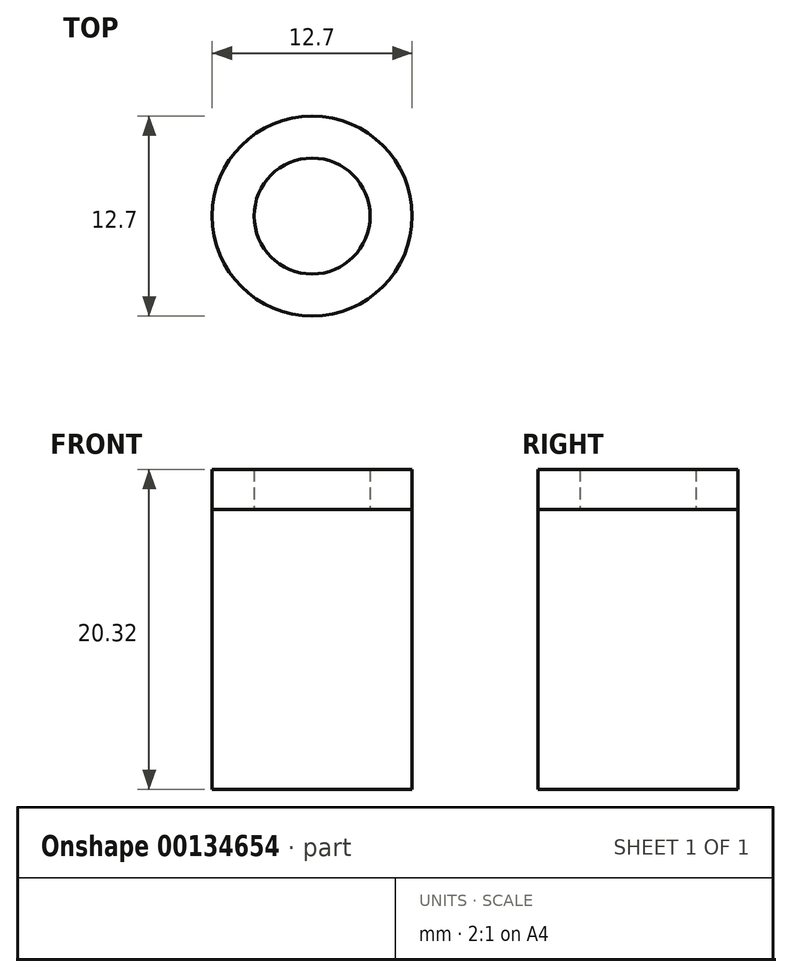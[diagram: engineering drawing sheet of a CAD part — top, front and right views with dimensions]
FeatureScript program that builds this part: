
annotation { "Feature Type Name" : "Feature", "Feature Type Description" : "" }
export const myFeature = defineFeature(function(context is Context, id is Id, definition is map)
    precondition{}
    {
        {
            var Q0;
            Q0=qCreatedBy(makeId("Top.planeOp"),FACE);
            var sketch = newSketch(context, id + "F0", { "sketchPlane" : qUnion([Q0])});
            skCircle(sketch, "E0", {"center": v(0, 0) * mm, "radius": 6.35 * mm});
            skSolve(sketch);
        }
        {
            var Q0;
            Q0=makeQuery(id+"F0.imprint","IMPRINT",FACE,{"disambiguationData":[TD([[makeQuery(id+"F0.imprint","IMPRINT",EDGE,{"derivedFrom":sQuery(id+"F0.wireOp",EDGE,"E0")}),1.0]])]});
            extrude(context, id + "F1", {"entities" : qUnion([Q0]), "depth" : 17.78 * mm});
        }
        {
            var Q0;
            Q0=makeQuery(id+"F1.opExtrude","CAP_FACE",FACE,{"disambiguationData":[OSD([sQuery(id+"F0.wireOp",EDGE,"E0")])],"isStart":false});
            var sketch = newSketch(context, id + "F2", { "sketchPlane" : qUnion([Q0])});
            skCircle(sketch, "E1", {"center": v(0, 0) * mm, "radius": 3.68 * mm});
            skSolve(sketch);
        }
        {
            var Q0;
            Q0=makeQuery(id+"F2.imprint","IMPRINT",FACE,{"disambiguationData":[TD([[makeQuery(id+"F2.imprint","IMPRINT",EDGE,{"derivedFrom":sQuery(id+"F2.wireOp",EDGE,"E1")}),1.0]])]});
            extrude(context, id + "F3", {"entities" : qUnion([Q0]), "depth" : 2.54 * mm});
        }
        {
            var Q0;
            Q0=makeQuery(id+"F1.opExtrude","CAP_FACE",FACE,{"disambiguationData":[OSD([sQuery(id+"F0.wireOp",EDGE,"E0")])],"isStart":false});
            extrude(context, id + "F4", {"entities" : qUnion([Q0]), "depth" : 2.54 * mm});
        }
    });
